# Revit family: QF_ZANUSSI_352085_Z2VVBDBRZA
name_source: partatom
category: Specialty Equipment
revit_build: Autodesk Revit 2018 (Build: 20190510_1515(x64)
units: mm (PartAtom-declared; Revit-internal decimal feet)

## family parameters
Always vertical = Yes
Cut with Voids When Loaded = No
Part Type = Normal
Room Calculation Point = No
Round Connector Dimension = Use Diameter
Shared = No
Work Plane-Based = No

## types (1)
- Standard
    Cold Water Size = 0 mm
    Compressed Air Pressure = 0.0 Pa
    Compressed Air Size = 0 mm
    Compressed Air Volume = 0.0 L/s
    Condensate Return Size = 0 mm
    Cycle = 60 Hz
    Description = LIBEROPRO POINT MOBILE COUNTER, 1 REFRIGERATED DRAWER,SUITABLE FOR 2 LIBEROPRO LINE APPLIANCES WITH FOUR 1-PHASE SOCKETS
    Direct Waste Size = 0 mm
    Gas KW = 0
    Gas Size = 0 mm
    HP = 20.1 HP
    Hot Water Size = 0 mm
    Item Number = 351084
    Manufacturer = Electrolux Professional
    Model = E2VVADBRZA
    Phase = 3
    Steam Pounds per Hour = 0
    Steam Supply Maximum Pressure = 0.0 Pa
    Steam Supply Minimum Pressure = 0.0 Pa
    Steam Supply Size = 0 mm
    URL = http://professional.electrolux.com
    Volts = 380 V
    Watts = 0 W

## geometry (parser evidence)
native form markers: Blend x2, Sweep x3
no freeform markers — native parametric forms only
